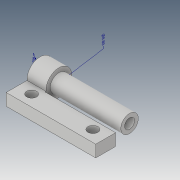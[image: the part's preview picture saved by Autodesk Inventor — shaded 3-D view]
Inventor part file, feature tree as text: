
AUTODESK INVENTOR PART (.ipt)
format: ipt  version: 2019 (Build 230136000, 136)  size: 183,808 bytes
history: native  units: mm
features: extrude x7, other x6, sketch x6, plane x5, move_body x2, fillet x1, direct_edit x1, projected_geometry x1
ambient origin geometry x8: Origin, YZ Plane, XZ Plane, XY Plane, X Axis, Y Axis, Z Axis, Center Point
bodies: Solid1 (feature_tree)
feature tree (29):
  other  "Annotations"
  extrude  "Extrusion1"  Depth=45.0mm
  sketch  "Sketch4"  dims[d5=5.0mm d6=5.0mm d7=11.0mm]
  extrude  "Extrusion4"  Depth=5.0mm
  fillet  "Fillet1"  Radius=11.0mm
  extrude  "Extrusion5"  Depth=23.0mm
  plane  "Work Plane1"
  extrude  "Extrusion6"  Depth=10.0mm
  plane  "Work Plane8"
  plane  "Work Plane10"
  sketch  "Sketch11"  dims[d24=3.0mm d25=0.0mm d26=12.0mm]
  plane  "Work Plane11"
  plane  "Work Plane12"
  extrude  "Extrusion10"  Depth=12.0mm
  extrude  "Extrusion11"  Depth=6.5mm TaperAngle=0.0deg
  direct_edit  "Direct Edit1"
  extrude  "Extrusion13"  Depth=6.5mm
  sketch  "Sketch1"  dims[d0=6.0mm d1=0.0mm d4=45.0mm]
  sketch  "Sketch5"  dims[d8=11.0mm d9=23.0mm]
  sketch  "Sketch6"  dims[d10=10.0mm d20=13.0mm]
  projected_geometry  "Projected Loop4"
  sketch  "Sketch13"  dims[d27=5.0mm d28=3.0mm d29=0.0mm d33=5.0mm d34=5.0mm d35=17.8mm d36=7.0mm d37=17.8mm d38=7.1mm d39=30.8mm d40=7.1mm d41=3.0mm d42=0.0mm d52=0.0mm d53=0.0mm d54=0.0mm d55=10.0mm d56=0.0mm d57=10.0mm d58=0.0mm d59=0.0mm d60=0.0mm d61=-1.5mm d62=0.0mm d63=0.0mm d64=-17.25mm d69=10.0mm d70=0.0mm d78=8.8mm d71=35.626875mm d72=6.5mm d75=48.705644mm d76=8.8mm]
  move_body  "Move1"
  move_body  "Move2"
  other  "Radial Dimension 1"
  other  "Diameter Dimension 1"
  parser-record x1  (decoder bookkeeping rows leaked as tree rows — omitted from the tree; the rows remain in map.json)
  other  "Cerniera Assemb.iam"
  other  "Cerniera 1:2"
note: 1 file-system path scrubbed to <path> (originals preserved in map.json)
